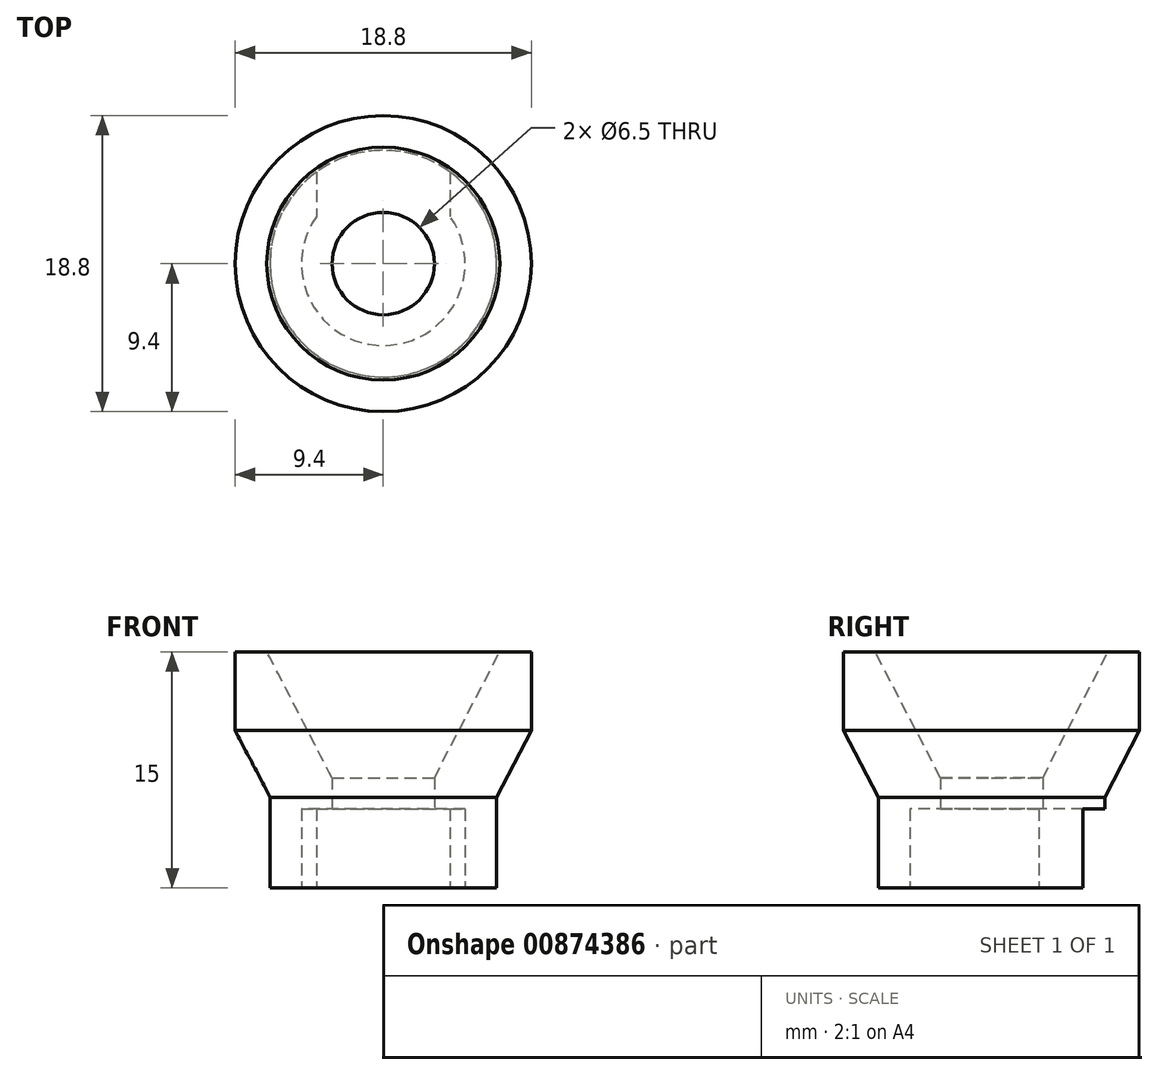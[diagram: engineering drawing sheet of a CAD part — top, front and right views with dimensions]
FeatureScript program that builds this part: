
annotation { "Feature Type Name" : "Feature", "Feature Type Description" : "" }
export const myFeature = defineFeature(function(context is Context, id is Id, definition is map)
    precondition{}
    {
        {
            var Q0;
            Q0=qCreatedBy(makeId("Front.planeOp"),FACE);
            var sketch = newSketch(context, id + "F0", { "sketchPlane" : qUnion([Q0])});
            skLineSegment(sketch, "E0", {"start": v(9.4, 10) * mm, "end": v(9.4, 15) * mm});
            skLineSegment(sketch, "E1", {"start": v(9.4, 15) * mm, "end": v(7.4, 15) * mm});
            skLineSegment(sketch, "E2", {"start": v(0, 0) * mm, "end": v(0, 10) * mm, "construction": true});
            skLineSegment(sketch, "E3", {"start": v(3.25, 5) * mm, "end": v(5.2, 5) * mm});
            skLineSegment(sketch, "E4", {"start": v(5.2, 5) * mm, "end": v(5.2, 0) * mm});
            skLineSegment(sketch, "E5", {"start": v(5.2, 0) * mm, "end": v(7.2, 0) * mm});
            skLineSegment(sketch, "E6", {"start": v(7.2, 0) * mm, "end": v(7.2, 5.76) * mm});
            skLineSegment(sketch, "E7", {"start": v(9.4, 10) * mm, "end": v(7.2, 5.76) * mm});
            skLineSegment(sketch, "E8", {"start": v(3.25, 5) * mm, "end": v(3.25, 7) * mm});
            skLineSegment(sketch, "E9", {"start": v(7.4, 15) * mm, "end": v(3.25, 7) * mm});
            skSolve(sketch);
        }
        {
            var Q0;
            Q0 = qSketchRegion(id + "F0", true);
            var Q1;
            Q1=sQuery(id+"F0.wireOp",EDGE,"E2");
            revolve(context, id + "F1", {"surfaceOperationType" : NewSurfaceOperationType.NEW, "entities" : qUnion([Q0]), "axis" : qUnion([Q1]), "revolveType" : RevolveType.FULL});
        }
        {
            var Q0;
            Q0=qCreatedBy(makeId("Front.planeOp"),FACE);
            var sketch = newSketch(context, id + "F2", { "sketchPlane" : qUnion([Q0])});
            skLineSegment(sketch, "E10.top", {"start": v(-4.25, 5) * mm, "end": v(4.25, 5) * mm});
            skLineSegment(sketch, "E10.left", {"start": v(-4.25, 0) * mm, "end": v(-4.25, 5) * mm});
            skLineSegment(sketch, "E10.right", {"start": v(4.25, 0) * mm, "end": v(4.25, 5) * mm});
            skLineSegment(sketch, "E11", {"start": v(-4.25, 0) * mm, "end": v(0, 0) * mm});
            skLineSegment(sketch, "E12", {"start": v(0, 0) * mm, "end": v(4.25, 0) * mm});
            skSolve(sketch);
        }
        {
            var Q0;
            Q0 = qSketchRegion(id + "F2", true);
            extrude(context, id + "F3", {"entities" : qUnion([Q0]), "operationType" : NewBodyOperationType.REMOVE, "oppositeDirection" : true, "depth" : 25 * mm, "offsetDistance" : 25 * mm});
        }
        {
            var Q0;
            Q0=makeQuery(id+"F3.boolean.opBoolean","MERGE",FACE,{"derivedFrom":[makeQuery(id+"F1.opRevolve","SWEPT_FACE",FACE,{"disambiguationData":[OSD([sQuery(id+"F0.wireOp",EDGE,"E3")])]})],"fromTools":[makeQuery(id+"F3.opExtrude","SWEPT_FACE",FACE,{"disambiguationData":[OSD([sQuery(id+"F2.wireOp",EDGE,"E10.top")])]})]});
            cPlane(context, id + "F4", {"entities" : qUnion([Q0]), "cplaneType" : CPlaneType.OFFSET, "offset" : 2 * mm, "oppositeDirection" : true, "width" : 150 * mm, "height" : 150 * mm});
        }
    });
